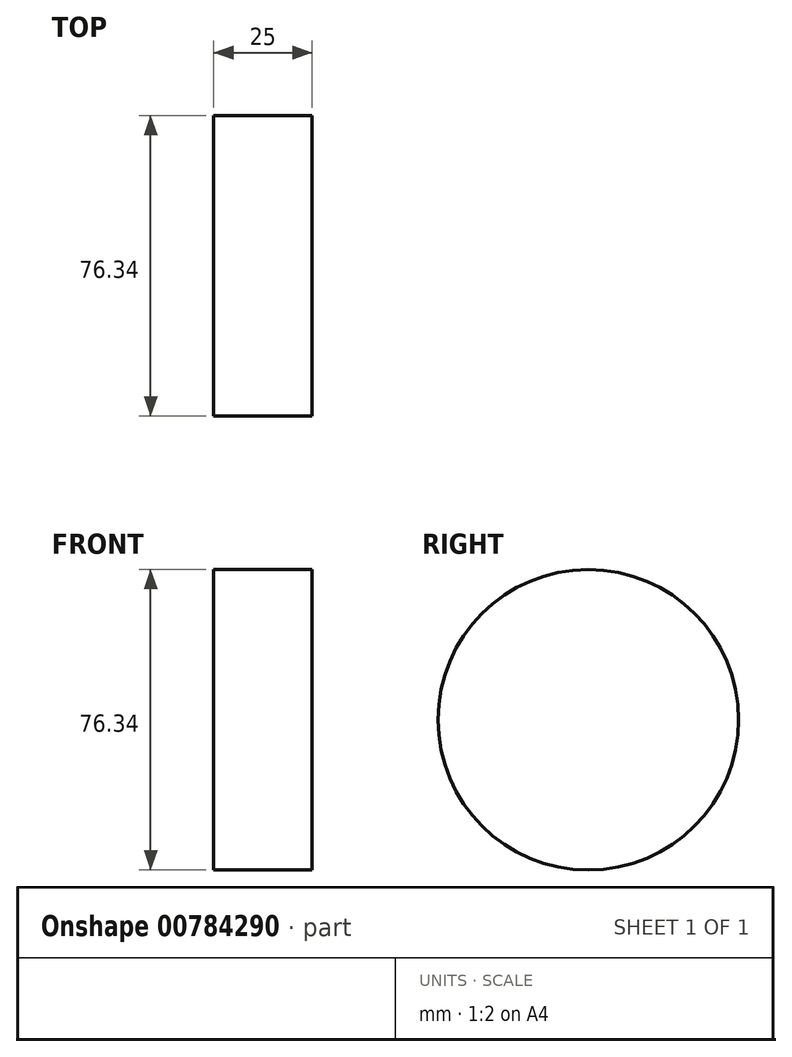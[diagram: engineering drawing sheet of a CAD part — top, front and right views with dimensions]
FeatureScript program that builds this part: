
annotation { "Feature Type Name" : "Feature", "Feature Type Description" : "" }
export const myFeature = defineFeature(function(context is Context, id is Id, definition is map)
    precondition{}
    {
        {
            var Q0;
            Q0=qCreatedBy(makeId("Right.planeOp"),FACE);
            var sketch = newSketch(context, id + "F0", { "sketchPlane" : qUnion([Q0])});
            skCircle(sketch, "E0", {"center": v(0, 0) * mm, "radius": 38.17 * mm});
            skSolve(sketch);
        }
        {
            var Q0;
            Q0=makeQuery(id+"F0.imprint","IMPRINT",FACE,{"disambiguationData":[TD([[makeQuery(id+"F0.imprint","IMPRINT",EDGE,{"derivedFrom":sQuery(id+"F0.wireOp",EDGE,"E0")}),1.0]])]});
            extrude(context, id + "F1", {"entities" : qUnion([Q0]), "depth" : 25 * mm, "offsetDistance" : 25 * mm});
        }
    });
